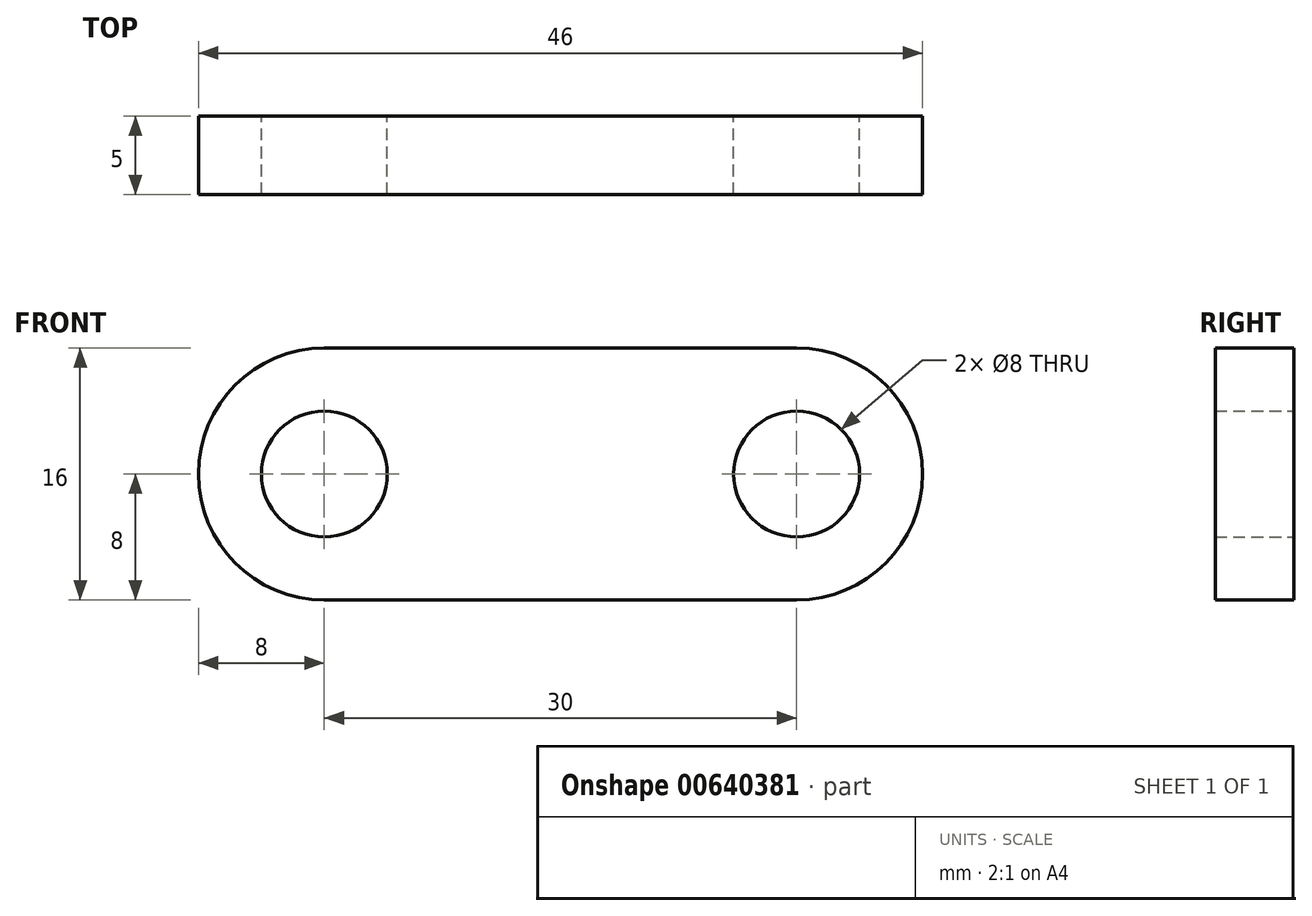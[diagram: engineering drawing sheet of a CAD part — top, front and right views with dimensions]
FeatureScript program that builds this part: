
annotation { "Feature Type Name" : "Feature", "Feature Type Description" : "" }
export const myFeature = defineFeature(function(context is Context, id is Id, definition is map)
    precondition{}
    {
        {
            var Q0;
            Q0=qCreatedBy(makeId("Front.planeOp"),FACE);
            var sketch = newSketch(context, id + "F0", { "sketchPlane" : qUnion([Q0])});
            skArc(sketch, "E0", {"start": v(-15, 8) * mm, "mid": v(-23, 0) * mm, "end": v(-15, -8) * mm});
            skLineSegment(sketch, "E1.bottom", {"start": v(-15, 8) * mm, "end": v(0, 8) * mm});
            skLineSegment(sketch, "E1.top", {"start": v(-15, -8) * mm, "end": v(0, -8) * mm});
            skLineSegment(sketch, "E1.right", {"start": v(0, 8) * mm, "end": v(0, -8) * mm});
            skCircle(sketch, "E2", {"center": v(-15, 0) * mm, "radius": 4 * mm});
            skSolve(sketch);
        }
        {
            var Q0;
            Q0=makeQuery(id+"F0.imprint","IMPRINT",FACE,{"disambiguationData":[TD([[makeQuery(id+"F0.imprint","IMPRINT",EDGE,{"derivedFrom":sQuery(id+"F0.wireOp",EDGE,"E0")}),1.0]])]});
            extrude(context, id + "F1", {"entities" : qUnion([Q0]), "endBound" : BoundingType.SYMMETRIC, "depth" : 5 * mm, "offsetDistance" : 25 * mm});
        }
        {
            var Q0;
            Q0=makeQuery(id+"F1.opExtrude","SWEPT_BODY",BODY,{"disambiguationData":[OSD([sQuery(id+"F0.wireOp",EDGE,"E0"),sQuery(id+"F0.wireOp",EDGE,"E1.bottom"),sQuery(id+"F0.wireOp",EDGE,"E1.top"),sQuery(id+"F0.wireOp",EDGE,"E1.right"),sQuery(id+"F0.wireOp",EDGE,"E2")])]});
            var Q1;
            Q1=makeQuery(id+"F1.opExtrude","SWEPT_FACE",FACE,{"disambiguationData":[OSD([sQuery(id+"F0.wireOp",EDGE,"E1.right")])]});
            mirror(context, id + "F2", {"operationType" : NewBodyOperationType.ADD, "entities" : qUnion([Q0]), "mirrorPlane" : qUnion([Q1])});
        }
    });
